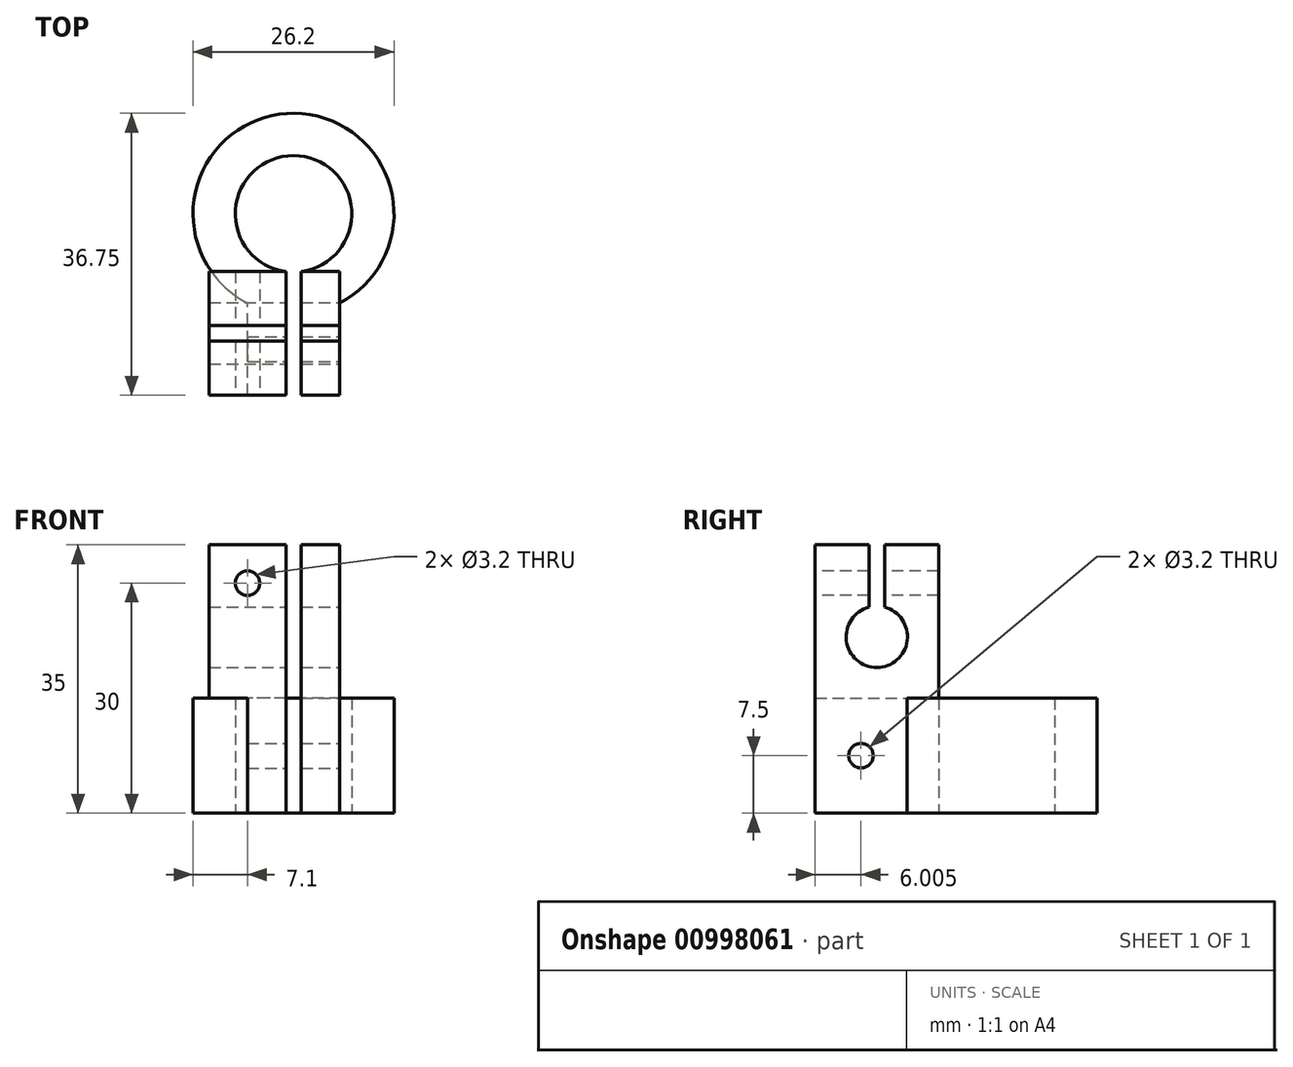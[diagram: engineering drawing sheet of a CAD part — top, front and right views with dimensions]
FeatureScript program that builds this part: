
annotation { "Feature Type Name" : "Feature", "Feature Type Description" : "" }
export const myFeature = defineFeature(function(context is Context, id is Id, definition is map)
    precondition{}
    {
        {
            var Q0;
            Q0=qCreatedBy(makeId("Top.planeOp"),FACE);
            var sketch = newSketch(context, id + "F0", { "sketchPlane" : qUnion([Q0])});
            skCircle(sketch, "E0", {"center": v(0, 0) * mm, "radius": 7.6 * mm});
            skCircle(sketch, "E1", {"center": v(0, 0) * mm, "radius": 13.1 * mm});
            skLineSegment(sketch, "E2.bottom", {"start": v(-6, -11.65) * mm, "end": v(6, -11.65) * mm, "construction": true});
            skLineSegment(sketch, "E2.top", {"start": v(-6, -23.65) * mm, "end": v(6, -23.65) * mm});
            skLineSegment(sketch, "E2.left", {"start": v(-6, -11.65) * mm, "end": v(-6, -23.65) * mm});
            skLineSegment(sketch, "E2.right", {"start": v(6, -11.65) * mm, "end": v(6, -23.65) * mm});
            skLineSegment(sketch, "E3.bottom", {"start": v(-1, -7.53) * mm, "end": v(1, -7.53) * mm});
            skLineSegment(sketch, "E3.top", {"start": v(-1, -23.65) * mm, "end": v(1, -23.65) * mm});
            skLineSegment(sketch, "E3.left", {"start": v(-1, -7.53) * mm, "end": v(-1, -23.65) * mm});
            skLineSegment(sketch, "E3.right", {"start": v(1, -7.53) * mm, "end": v(1, -23.65) * mm});
            skSolve(sketch);
        }
        {
            var Q0;
            {var subQ0=sQuery(id+"F0.wireOp",EDGE,"E2.left");Q0=makeQuery(id+"F0.imprint","IMPRINT",FACE,{"disambiguationData":[TD([[makeQuery(id+"F0.imprint","IMPRINT",EDGE,{"derivedFrom":subQ0}),1.0]])]});}
            var Q1;
            {var subQ0=sQuery(id+"F0.wireOp",EDGE,"E2.right");Q1=makeQuery(id+"F0.imprint","IMPRINT",FACE,{"disambiguationData":[TD([[makeQuery(id+"F0.imprint","IMPRINT",EDGE,{"derivedFrom":subQ0}),-1.0]])]});}
            var Q2;
            {var subQ0=sQuery(id+"F0.wireOp",EDGE,"E1");var subQ1=makeQuery(id+"F0.imprint","INTERSECT",VERTEX,{"derivedFrom":[subQ0,sQuery(id+"F0.wireOp",EDGE,"E2.left")]});Q2=makeQuery(id+"F0.imprint","IMPRINT",FACE,{"disambiguationData":[TD([[makeQuery(id+"F0.imprint","IMPRINT",EDGE,{"disambiguationData":[TD([[subQ1,-1.0]])],"derivedFrom":subQ0}),1.0]])]});}
            extrude(context, id + "F1", {"entities" : qUnion([Q0, Q1, Q2]), "depth" : 15 * mm, "offsetDistance" : 25 * mm});
        }
        {
            var Q0;
            Q0=makeQuery(id+"F1.opExtrude","SWEPT_FACE",FACE,{"disambiguationData":[OSD([sQuery(id+"F0.wireOp",EDGE,"E2.right")])]});
            var sketch = newSketch(context, id + "F2", { "sketchPlane" : qUnion([Q0])});
            skLineSegment(sketch, "E4", {"start": v(-17.65, 15) * mm, "end": v(-17.65, 0) * mm, "construction": true});
            skCircle(sketch, "E5", {"center": v(-17.65, 7.5) * mm, "radius": 1.6 * mm});
            skSolve(sketch);
        }
        {
            var Q0;
            Q0 = qSketchRegion(id + "F2", true);
            extrude(context, id + "F3", {"entities" : qUnion([Q0]), "operationType" : NewBodyOperationType.REMOVE, "oppositeDirection" : true, "depth" : 20 * mm, "offsetDistance" : 25 * mm});
        }
        {
            var Q0;
            Q0=makeQuery(id+"F1.opExtrude","CAP_FACE",FACE,{"disambiguationData":[OSD([sQuery(id+"F0.wireOp",EDGE,"E0"),sQuery(id+"F0.wireOp",EDGE,"E1"),sQuery(id+"F0.wireOp",EDGE,"E2.top"),sQuery(id+"F0.wireOp",EDGE,"E2.left"),sQuery(id+"F0.wireOp",EDGE,"E2.right"),sQuery(id+"F0.wireOp",EDGE,"E3.left"),sQuery(id+"F0.wireOp",EDGE,"E3.right")])],"isStart":false});
            var sketch = newSketch(context, id + "F4", { "sketchPlane" : qUnion([Q0])});
            skLineSegment(sketch, "E6.bottom", {"start": v(1, -7.53) * mm, "end": v(6, -7.53) * mm});
            skLineSegment(sketch, "E6.top", {"start": v(1, -23.65) * mm, "end": v(6, -23.65) * mm});
            skLineSegment(sketch, "E6.left", {"start": v(1, -7.53) * mm, "end": v(1, -23.65) * mm});
            skLineSegment(sketch, "E6.right", {"start": v(6, -7.53) * mm, "end": v(6, -23.65) * mm});
            skLineSegment(sketch, "E7.bottom", {"start": v(-1, -7.53) * mm, "end": v(-6, -7.53) * mm});
            skLineSegment(sketch, "E7.top", {"start": v(-1, -23.65) * mm, "end": v(-6, -23.65) * mm});
            skLineSegment(sketch, "E7.left", {"start": v(-1, -7.53) * mm, "end": v(-1, -23.65) * mm});
            skLineSegment(sketch, "E7.right", {"start": v(-6, -7.53) * mm, "end": v(-6, -23.65) * mm});
            skSolve(sketch);
        }
        {
            var Q0;
            Q0 = qSketchRegion(id + "F4", true);
            extrude(context, id + "F5", {"entities" : qUnion([Q0]), "operationType" : NewBodyOperationType.ADD, "depth" : 20 * mm, "offsetDistance" : 25 * mm});
        }
        {
            var Q0;
            Q0=makeQuery(id+"F5.boolean.opBoolean","MERGE",FACE,{"derivedFrom":[makeQuery(id+"F1.opExtrude","SWEPT_FACE",FACE,{"disambiguationData":[OSD([sQuery(id+"F0.wireOp",EDGE,"E2.left")])]}),makeQuery(id+"F5.opExtrude","SWEPT_FACE",FACE,{"disambiguationData":[OSD([sQuery(id+"F4.wireOp",EDGE,"E7.right")])]})]});
            var sketch = newSketch(context, id + "F6", { "sketchPlane" : qUnion([Q0])});
            skLineSegment(sketch, "E8.bottom", {"start": v(23.65, 35) * mm, "end": v(7.53, 35) * mm});
            skLineSegment(sketch, "E8.top", {"start": v(23.65, 15) * mm, "end": v(7.53, 15) * mm});
            skLineSegment(sketch, "E8.left", {"start": v(23.65, 35) * mm, "end": v(23.65, 15) * mm});
            skLineSegment(sketch, "E8.right", {"start": v(7.53, 35) * mm, "end": v(7.53, 15) * mm});
            skSolve(sketch);
        }
        {
            var Q0;
            Q0 = qSketchRegion(id + "F6", true);
            extrude(context, id + "F7", {"entities" : qUnion([Q0]), "operationType" : NewBodyOperationType.ADD, "depth" : 5 * mm, "offsetDistance" : 25 * mm});
        }
        {
            var Q0;
            Q0=makeQuery(id+"F5.boolean.opBoolean","MERGE",FACE,{"derivedFrom":[makeQuery(id+"F1.opExtrude","SWEPT_FACE",FACE,{"disambiguationData":[OSD([sQuery(id+"F0.wireOp",EDGE,"E2.right")])]}),makeQuery(id+"F5.opExtrude","SWEPT_FACE",FACE,{"disambiguationData":[OSD([sQuery(id+"F4.wireOp",EDGE,"E6.right")])]})]});
            var sketch = newSketch(context, id + "F8", { "sketchPlane" : qUnion([Q0])});
            skLineSegment(sketch, "E9", {"start": v(-15.59, 35) * mm, "end": v(-15.59, 0) * mm, "construction": true});
            skCircle(sketch, "E10", {"center": v(-15.59, 23) * mm, "radius": 4 * mm});
            skLineSegment(sketch, "E11.bottom", {"start": v(-16.59, 35) * mm, "end": v(-14.59, 35) * mm});
            skLineSegment(sketch, "E11.top", {"start": v(-16.59, 26.87) * mm, "end": v(-14.59, 26.87) * mm});
            skLineSegment(sketch, "E11.left", {"start": v(-16.59, 35) * mm, "end": v(-16.59, 26.87) * mm});
            skLineSegment(sketch, "E11.right", {"start": v(-14.59, 35) * mm, "end": v(-14.59, 26.87) * mm});
            skSolve(sketch);
        }
        {
            var Q0;
            Q0 = qSketchRegion(id + "F8", true);
            extrude(context, id + "F9", {"entities" : qUnion([Q0]), "operationType" : NewBodyOperationType.REMOVE, "oppositeDirection" : true, "depth" : 20 * mm, "offsetDistance" : 25 * mm});
        }
        {
            var Q0;
            {var subQ0=sQuery(id+"F0.wireOp",EDGE,"E2.top");Q0=makeQuery(id+"F7.boolean.opBoolean","MERGE",FACE,{"derivedFrom":[makeQuery(id+"F5.boolean.opBoolean","MERGE",FACE,{"derivedFrom":[makeQuery(id+"F1.opExtrude","SWEPT_FACE",FACE,{"disambiguationData":[OSD([subQ0]),TDD([makeQuery(id+"F0.imprint","IMPRINT",EDGE,{"disambiguationData":[TD([[makeQuery(id+"F0.imprint","INTERSECT",VERTEX,{"derivedFrom":[subQ0,sQuery(id+"F0.wireOp",EDGE,"E2.left")]}),-1.0]])],"derivedFrom":subQ0})])]}),makeQuery(id+"F5.opExtrude","SWEPT_FACE",FACE,{"disambiguationData":[OSD([sQuery(id+"F4.wireOp",EDGE,"E7.top")])]})]}),makeQuery(id+"F7.opExtrude","SWEPT_FACE",FACE,{"disambiguationData":[OSD([sQuery(id+"F6.wireOp",EDGE,"E8.left")])]})]});}
            var sketch = newSketch(context, id + "F10", { "sketchPlane" : qUnion([Q0])});
            skLineSegment(sketch, "E12", {"start": v(-11, 30) * mm, "end": v(-1, 30) * mm, "construction": true});
            skCircle(sketch, "E13", {"center": v(-6, 30) * mm, "radius": 1.6 * mm});
            skSolve(sketch);
        }
        {
            var Q0;
            Q0 = qSketchRegion(id + "F10", true);
            extrude(context, id + "F11", {"entities" : qUnion([Q0]), "operationType" : NewBodyOperationType.REMOVE, "oppositeDirection" : true, "depth" : 20 * mm, "offsetDistance" : 25 * mm});
        }
    });
